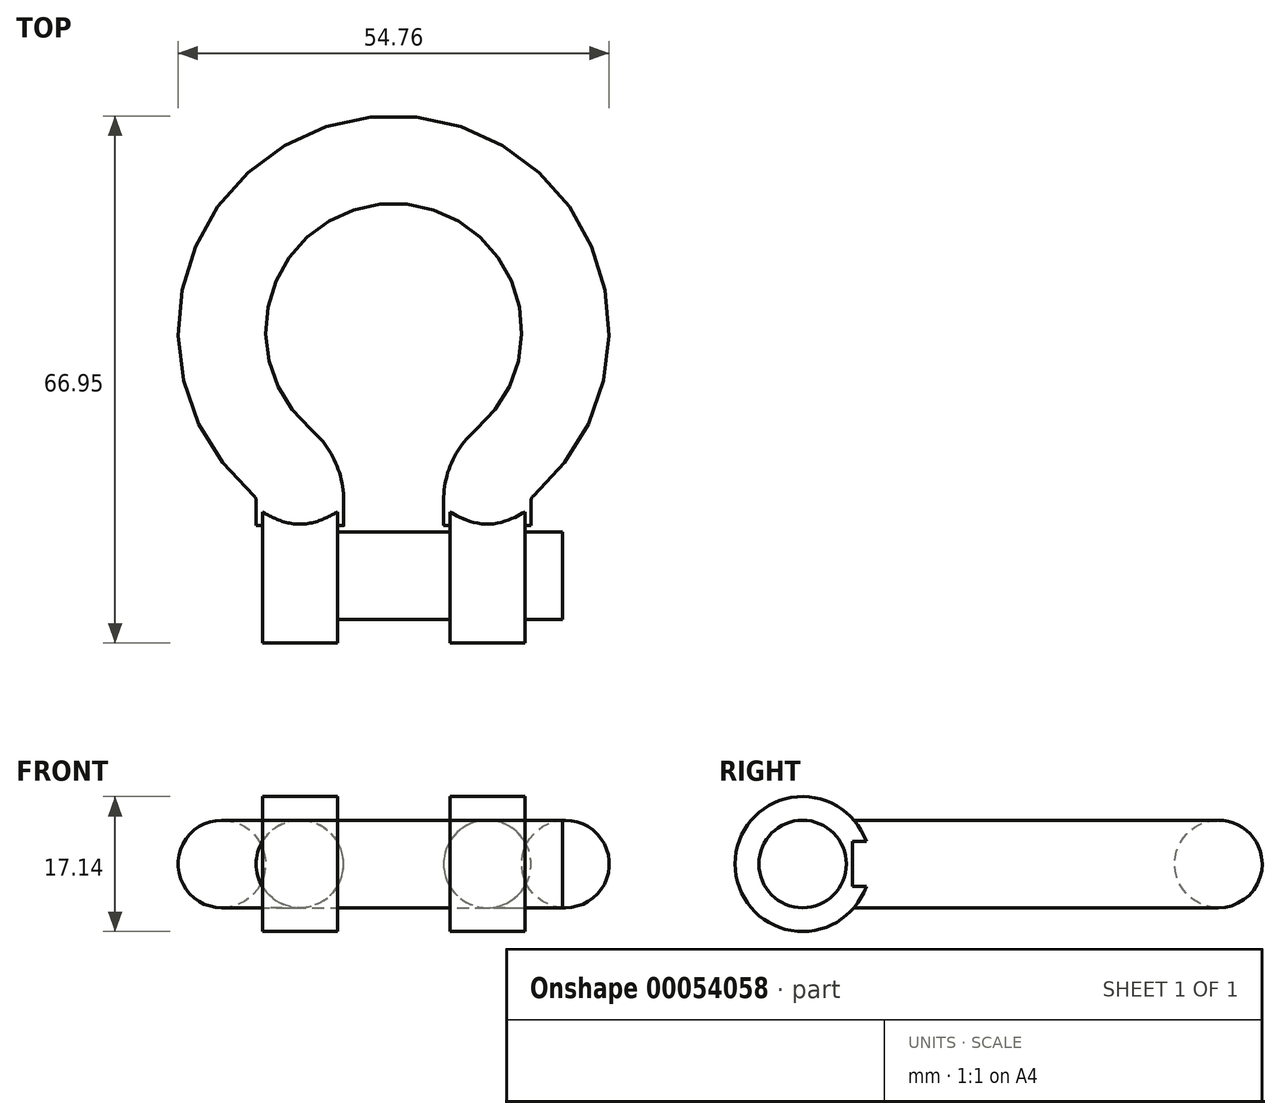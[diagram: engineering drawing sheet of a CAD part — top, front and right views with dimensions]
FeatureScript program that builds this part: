
annotation { "Feature Type Name" : "Feature", "Feature Type Description" : "" }
export const myFeature = defineFeature(function(context is Context, id is Id, definition is map)
    precondition{}
    {
        {
            var Q0;
            Q0=qCreatedBy(makeId("Top.planeOp"),FACE);
            var sketch = newSketch(context, id + "F0", { "sketchPlane" : qUnion([Q0])});
            skArc(sketch, "E0", {"start": v(14.14, -16.63) * mm, "mid": v(0, 21.83) * mm, "end": v(-14.14, -16.63) * mm});
            skLineSegment(sketch, "E1.rect.right", {"start": v(-11.9, -24.65) * mm, "end": v(-11.9, -21.46) * mm});
            skLineSegment(sketch, "E2", {"start": v(11.9, -24.65) * mm, "end": v(11.9, -21.46) * mm});
            skPoint(sketch, "E3", {"position": v(0, -24.65) * mm});
            skPoint(sketch, "E4.visualSharp", {"position": v(11.9, -18.3) * mm});
            skArc(sketch, "E4.filletArc", {"start": v(14.14, -16.63) * mm, "mid": v(12.5, -18.8) * mm, "end": v(11.9, -21.46) * mm});
            skPoint(sketch, "E5.visualSharp", {"position": v(-11.9, -18.3) * mm});
            skArc(sketch, "E5.filletArc", {"start": v(-11.9, -21.46) * mm, "mid": v(-12.5, -18.8) * mm, "end": v(-14.14, -16.63) * mm});
            skSolve(sketch);
        }
        {
            var Q0;
            Q0=sQuery(id+"F0.wireOp",VERTEX,"E1.rect.right.start");
            var Q1;
            Q1=sQuery(id+"F0.wireOp",EDGE,"E1.rect.right");
            cPlane(context, id + "F1", {"entities" : qUnion([Q0, Q1]), "cplaneType" : CPlaneType.LINE_POINT, "offset" : 152.4 * mm, "width" : 152.4 * mm, "height" : 152.4 * mm});
        }
        {
            var Q0;
            Q0=qCreatedBy(id+"F1.planeOp",FACE);
            var sketch = newSketch(context, id + "F2", { "sketchPlane" : qUnion([Q0])});
            skCircle(sketch, "E6", {"center": v(11.9, 0) * mm, "radius": 5.56 * mm});
            skSolve(sketch);
        }
        {
            var Q0;
            Q0=makeQuery(id+"F2.imprint","IMPRINT",FACE,{"disambiguationData":[TD([[makeQuery(id+"F2.imprint","IMPRINT",EDGE,{"derivedFrom":sQuery(id+"F2.wireOp",EDGE,"E6")}),1.0]])]});
            var Q1;
            Q1=sQuery(id+"F0.wireOp",EDGE,"E1.rect.right");
            var Q2;
            Q2=sQuery(id+"F0.wireOp",EDGE,"E5.filletArc");
            var Q3;
            Q3=sQuery(id+"F0.wireOp",EDGE,"E0");
            var Q4;
            Q4=sQuery(id+"F0.wireOp",EDGE,"E4.filletArc");
            var Q5;
            Q5=sQuery(id+"F0.wireOp",EDGE,"E2");
            sweep(context, id + "F3", {"profiles" : qUnion([Q0]), "path" : qUnion([Q1, Q2, Q3, Q4, Q5])});
        }
        {
            var Q0;
            Q0=qCreatedBy(makeId("Right.planeOp"),FACE);
            var Q1;
            Q1=sQuery(id+"F2.wireOp",VERTEX,"E6.center");
            cPlane(context, id + "F4", {"entities" : qUnion([Q0, Q1]), "cplaneType" : CPlaneType.PLANE_POINT, "offset" : 152.4 * mm, "width" : 152.4 * mm, "height" : 152.4 * mm});
        }
        {
            var Q0;
            Q0=qCreatedBy(id+"F4.planeOp",FACE);
            var sketch = newSketch(context, id + "F5", { "sketchPlane" : qUnion([Q0])});
            skCircle(sketch, "E7", {"center": v(-31, 0) * mm, "radius": 8.57 * mm});
            skSolve(sketch);
        }
        {
            var Q0;
            Q0=makeQuery(id+"F5.imprint","IMPRINT",FACE,{"disambiguationData":[TD([[makeQuery(id+"F5.imprint","IMPRINT",EDGE,{"derivedFrom":sQuery(id+"F5.wireOp",EDGE,"E7")}),1.0]])]});
            extrude(context, id + "F6", {"entities" : qUnion([Q0]), "operationType" : NewBodyOperationType.ADD, "depth" : 9.52 * mm, "symmetric" : true});
        }
        {
            var Q0;
            Q0=makeQuery(id+"F3.opSweep","SWEPT_BODY",BODY,{"disambiguationData":[OSD([sQuery(id+"F0.wireOp",EDGE,"E2"),sQuery(id+"F2.wireOp",EDGE,"E6")])]});
            var Q1;
            Q1=qCreatedBy(makeId("Right.planeOp"),FACE);
            mirror(context, id + "F7", {"operationType" : NewBodyOperationType.ADD, "entities" : qUnion([Q0]), "mirrorPlane" : qUnion([Q1])});
        }
        {
            var Q0;
            Q0=makeQuery(id+"F6.opExtrude","CAP_FACE",FACE,{"disambiguationData":[OSD([sQuery(id+"F5.wireOp",EDGE,"E7")])],"isStart":true});
            var sketch = newSketch(context, id + "F8", { "sketchPlane" : qUnion([Q0])});
            skCircle(sketch, "E8", {"center": v(31, 0) * mm, "radius": 5.56 * mm});
            skSolve(sketch);
        }
        {
            var Q0;
            Q0=makeQuery(id+"F8.imprint","IMPRINT",FACE,{"disambiguationData":[TD([[makeQuery(id+"F8.imprint","IMPRINT",EDGE,{"derivedFrom":sQuery(id+"F8.wireOp",EDGE,"E8")}),1.0]])]});
            extrude(context, id + "F9", {"entities" : qUnion([Q0]), "operationType" : NewBodyOperationType.ADD, "oppositeDirection" : true, "depth" : 38.1 * mm});
        }
    });
